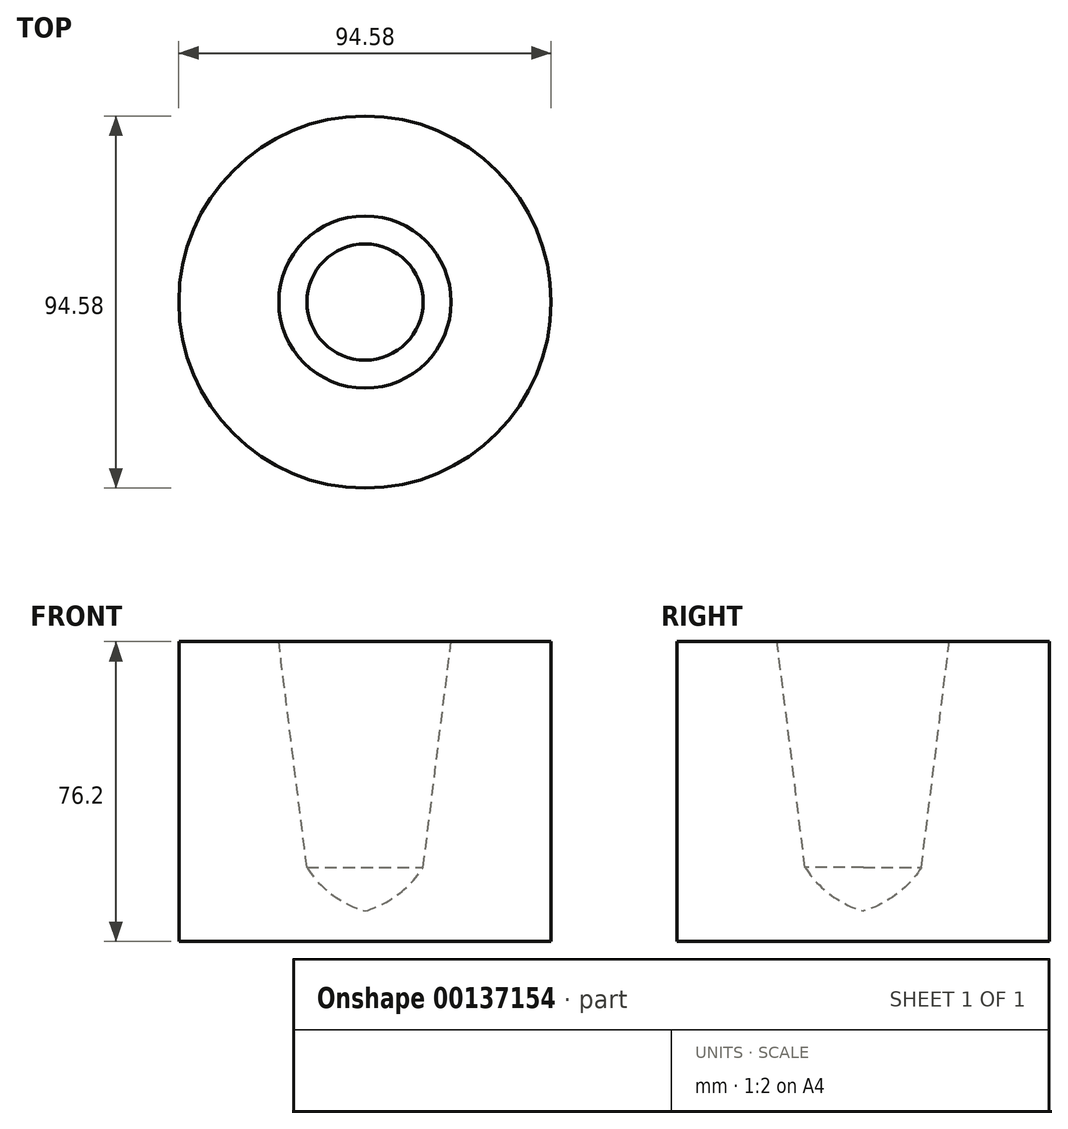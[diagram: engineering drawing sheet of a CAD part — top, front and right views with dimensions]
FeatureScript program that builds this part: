
annotation { "Feature Type Name" : "Feature", "Feature Type Description" : "" }
export const myFeature = defineFeature(function(context is Context, id is Id, definition is map)
    precondition{}
    {
        {
            var Q0;
            Q0=qCreatedBy(makeId("Front.planeOp"),FACE);
            var sketch = newSketch(context, id + "F0", { "sketchPlane" : qUnion([Q0])});
            skLineSegment(sketch, "E0", {"start": v(-21.89, 0) * mm, "end": v(-47.29, 0) * mm});
            skLineSegment(sketch, "E1", {"start": v(-47.29, 0) * mm, "end": v(-47.29, -76.2) * mm});
            skLineSegment(sketch, "E2", {"start": v(-47.29, -76.2) * mm, "end": v(0, -76.2) * mm});
            skLineSegment(sketch, "E3", {"start": v(0, -76.2) * mm, "end": v(0, -68.45) * mm});
            skLineSegment(sketch, "E4", {"start": v(-21.89, 0) * mm, "end": v(-14.77, -57.35) * mm});
            skArc(sketch, "E5", {"start": v(-14.77, -57.35) * mm, "mid": v(-8.39, -64.24) * mm, "end": v(0, -68.45) * mm});
            skSolve(sketch);
        }
        {
            var Q0;
            Q0 = qSketchRegion(id + "F0", true);
            var Q1;
            Q1=sQuery(id+"F0.wireOp",EDGE,"E3");
            revolve(context, id + "F1", {"entities" : qUnion([Q0]), "axis" : qUnion([Q1]), "revolveType" : RevolveType.FULL});
        }
    });
